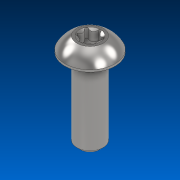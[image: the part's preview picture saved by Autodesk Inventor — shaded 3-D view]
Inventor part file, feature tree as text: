
AUTODESK INVENTOR PART (.ipt)
format: ipt  version: 2022.2 (Build 262287000, 287)  size: 184,832 bytes
history: native  units: in
note: dims shown in document units (in); Inventor stores cm internally (conversion verified against a paired STEP export)
features: direct_edit x1, chamfer x1, move_body x1
ambient origin geometry x8: Origin, YZ Plane, XZ Plane, XY Plane, X Axis, Y Axis, Z Axis, Center Point
bodies: Solid1 (feature_tree)
feature tree (3):
  direct_edit  "Direct Edit1"
  chamfer  "Chamfer2"  [1 undecoded]
  move_body  "Move1"
note: 1 required parameter value undecoded (feature->parameter linkage not recoverable at this tier; creation-order binding heuristic only, values carry confidence <= 0.55)
